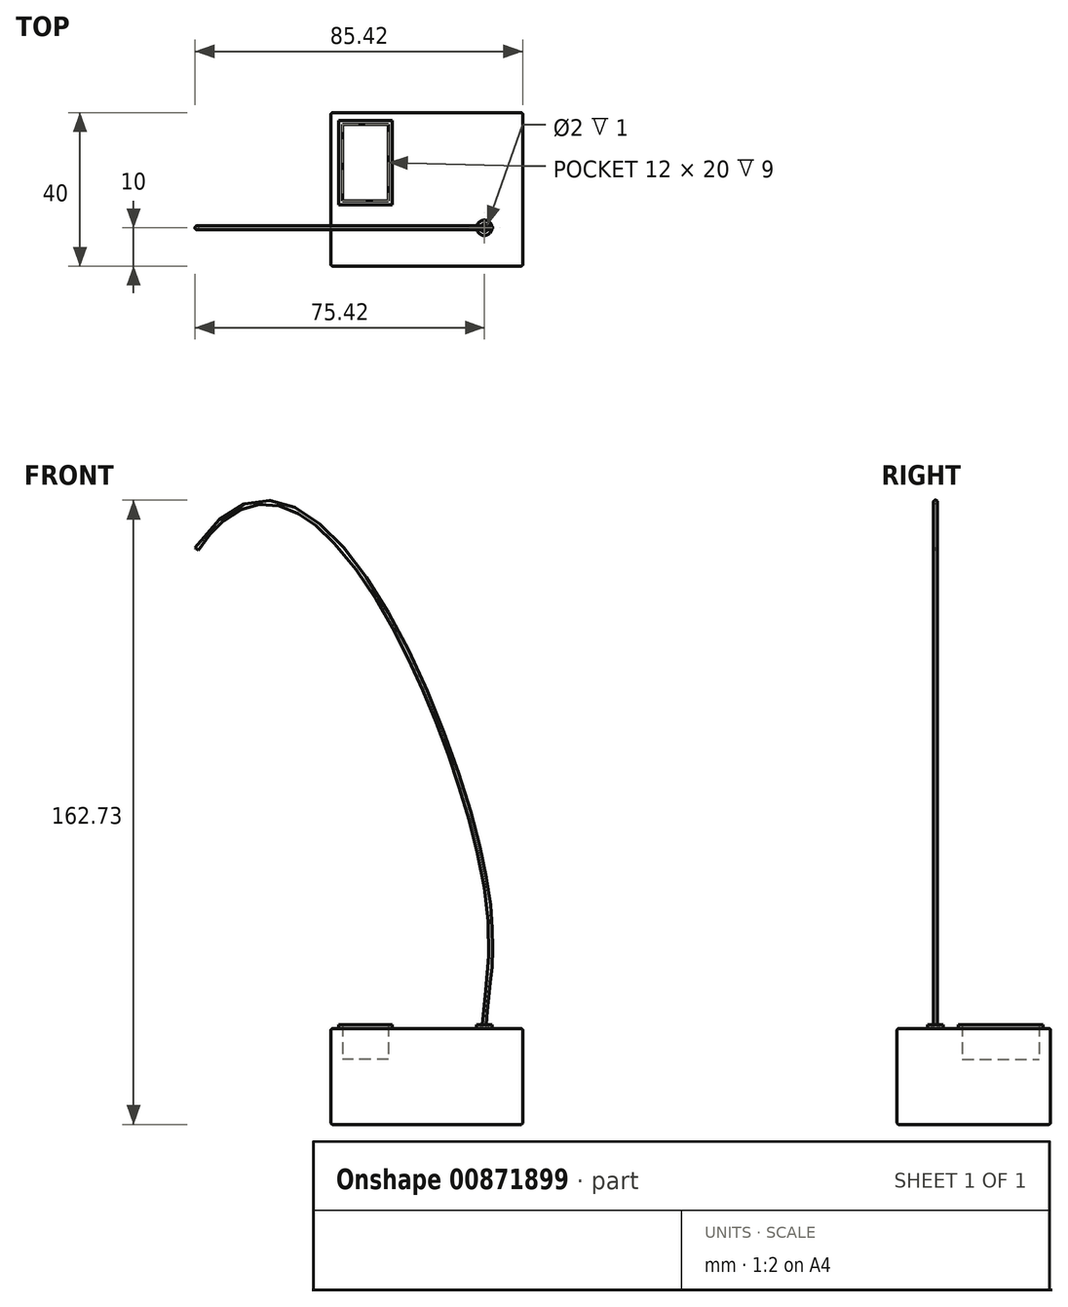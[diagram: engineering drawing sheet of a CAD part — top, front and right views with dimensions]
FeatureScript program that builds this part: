
annotation { "Feature Type Name" : "Feature", "Feature Type Description" : "" }
export const myFeature = defineFeature(function(context is Context, id is Id, definition is map)
    precondition{}
    {
        {
            var Q0;
            Q0=qCreatedBy(makeId("Top.planeOp"),FACE);
            var sketch = newSketch(context, id + "F0", { "sketchPlane" : qUnion([Q0])});
            skLineSegment(sketch, "E0.bottom", {"start": v(25, -20) * mm, "end": v(-25, -20) * mm});
            skLineSegment(sketch, "E0.top", {"start": v(25, 20) * mm, "end": v(-25, 20) * mm});
            skLineSegment(sketch, "E0.left", {"start": v(25, -20) * mm, "end": v(25, 20) * mm});
            skLineSegment(sketch, "E0.right", {"start": v(-25, -20) * mm, "end": v(-25, 20) * mm});
            skPoint(sketch, "E0.middle", {"position": v(0, 0) * mm});
            skSolve(sketch);
        }
        {
            var Q0;
            Q0=makeQuery(id+"F0.imprint","IMPRINT",FACE,{"disambiguationData":[TD([[makeQuery(id+"F0.imprint","IMPRINT",EDGE,{"derivedFrom":sQuery(id+"F0.wireOp",EDGE,"E0.bottom")}),-1.0]])]});
            extrude(context, id + "F1", {"entities" : qUnion([Q0]), "depth" : 25 * mm, "offsetDistance" : 25 * mm});
        }
        {
            var Q0;
            Q0=makeQuery(id+"F1.opExtrude","CAP_FACE",FACE,{"disambiguationData":[OSD([sQuery(id+"F0.wireOp",EDGE,"E0.bottom"),sQuery(id+"F0.wireOp",EDGE,"E0.top"),sQuery(id+"F0.wireOp",EDGE,"E0.left"),sQuery(id+"F0.wireOp",EDGE,"E0.right")])],"isStart":false});
            var sketch = newSketch(context, id + "F2", { "sketchPlane" : qUnion([Q0])});
            skLineSegment(sketch, "E1.bottom", {"start": v(-9, 18) * mm, "end": v(-23, 18) * mm});
            skLineSegment(sketch, "E1.top", {"start": v(-9, -4) * mm, "end": v(-23, -4) * mm});
            skLineSegment(sketch, "E1.left", {"start": v(-9, 18) * mm, "end": v(-9, -4) * mm});
            skLineSegment(sketch, "E1.right", {"start": v(-23, 18) * mm, "end": v(-23, -4) * mm});
            skPoint(sketch, "E1.middle", {"position": v(-16, 7) * mm});
            skLineSegment(sketch, "E2.bottom", {"start": v(-10, -3) * mm, "end": v(-22, -3) * mm});
            skLineSegment(sketch, "E2.top", {"start": v(-10, 17) * mm, "end": v(-22, 17) * mm});
            skLineSegment(sketch, "E2.left", {"start": v(-10, -3) * mm, "end": v(-10, 17) * mm});
            skLineSegment(sketch, "E2.right", {"start": v(-22, -3) * mm, "end": v(-22, 17) * mm});
            skCircle(sketch, "E3", {"center": v(15, -10) * mm, "radius": 2 * mm});
            skCircle(sketch, "E4", {"center": v(15, -10) * mm, "radius": 1 * mm});
            skSolve(sketch);
        }
        {
            var Q0;
            Q0=qSketchRegion(id+"F2",true);
            extrude(context, id + "F3", {"entities" : qUnion([Q0]), "operationType" : NewBodyOperationType.ADD, "depth" : 1 * mm, "offsetDistance" : 25 * mm});
        }
        {
            var Q0;
            Q0=makeQuery(id+"F3.boolean.opBoolean","SPLIT",FACE,{"disambiguationData":[TD([makeQuery(id+"F3.opExtrude","SWEPT_FACE",FACE,{"disambiguationData":[OSD([sQuery(id+"F2.wireOp",EDGE,"E2.bottom")])]})])],"derivedFrom":makeQuery(id+"F1.opExtrude","CAP_FACE",FACE,{"disambiguationData":[OSD([sQuery(id+"F0.wireOp",EDGE,"E0.bottom"),sQuery(id+"F0.wireOp",EDGE,"E0.top"),sQuery(id+"F0.wireOp",EDGE,"E0.left"),sQuery(id+"F0.wireOp",EDGE,"E0.right")])],"isStart":false})});
            extrude(context, id + "F4", {"entities" : qUnion([Q0]), "operationType" : NewBodyOperationType.REMOVE, "oppositeDirection" : true, "depth" : 8 * mm, "offsetDistance" : 25 * mm});
        }
        {
            var Q0;
            Q0=makeQuery(id+"F1.opExtrude","SWEPT_FACE",FACE,{"disambiguationData":[OSD([sQuery(id+"F0.wireOp",EDGE,"E0.bottom")])]});
            cPlane(context, id + "F5", {"entities" : qUnion([Q0]), "cplaneType" : CPlaneType.OFFSET, "offset" : 10 * mm, "oppositeDirection" : true, "width" : 150 * mm, "height" : 150 * mm});
        }
        {
            var Q0;
            Q0=qCreatedBy(id+"F5.planeOp",FACE);
            var sketch = newSketch(context, id + "F6", { "sketchPlane" : qUnion([Q0])});
            skLineSegment(sketch, "E5.0", {"start": v(13, 25) * mm, "end": v(17, 25) * mm, "construction": true});
            skFitSpline(sketch, "E6", {"points": [v(15, 25) * mm, v(13.23, 72.74) * mm, v(-60, 150) * mm], "startDerivative": vector(0, 83.51) * mm, "endDerivative": vector(-143.19, -213.8) * mm});
            skLineSegment(sketch, "E7", {"start": v(15, 25) * mm, "end": v(15, 12.73) * mm, "construction": true});
            skSolve(sketch);
        }
        {
            var Q0;
            {var subQ0=sQuery(id+"F0.wireOp",EDGE,"E0.left");var subQ1=sQuery(id+"F0.wireOp",EDGE,"E0.top");var subQ2=sQuery(id+"F0.wireOp",EDGE,"E0.right");var subQ3=sQuery(id+"F0.wireOp",EDGE,"E0.bottom");Q0=makeQuery(id+"F3.boolean.opBoolean","SPLIT",FACE,{"disambiguationData":[TD([makeQuery(id+"F1.opExtrude","SWEPT_FACE",FACE,{"disambiguationData":[OSD([subQ3])]})])],"derivedFrom":makeQuery(id+"F1.opExtrude","CAP_FACE",FACE,{"disambiguationData":[OSD([subQ3,subQ1,subQ0,subQ2])],"isStart":false})});}
            var sketch = newSketch(context, id + "F7", { "sketchPlane" : qUnion([Q0])});
            skCircle(sketch, "E8", {"center": v(15, -10) * mm, "radius": 0.5 * mm});
            skSolve(sketch);
        }
        {
            var Q0;
            Q0=qSketchRegion(id+"F7",true);
            var Q1;
            Q1=sQuery(id+"F6.wireOp",EDGE,"E6");
            var Q2;
            Q2=sQuery(id+"F6.wireOp",EDGE,"E6");
            sweep(context, id + "F8", {"operationType" : NewBodyOperationType.ADD, "profiles" : qUnion([Q0]), "surfaceProfiles" : qUnion([Q1]), "path" : qUnion([Q2])});
        }
        {
            var Q0;
            Q0=makeQuery(id+"F1.opExtrude","CAP_EDGE",EDGE,{"disambiguationData":[OSD([sQuery(id+"F0.wireOp",EDGE,"E0.top")])],"isStart":false});
            var Q1;
            Q1=makeQuery(id+"F1.opExtrude","CAP_EDGE",EDGE,{"disambiguationData":[OSD([sQuery(id+"F0.wireOp",EDGE,"E0.left")])],"isStart":false});
            var Q2;
            Q2=makeQuery(id+"F1.opExtrude","CAP_EDGE",EDGE,{"disambiguationData":[OSD([sQuery(id+"F0.wireOp",EDGE,"E0.bottom")])],"isStart":false});
            var Q3;
            Q3=makeQuery(id+"F1.opExtrude","CAP_EDGE",EDGE,{"disambiguationData":[OSD([sQuery(id+"F0.wireOp",EDGE,"E0.right")])],"isStart":false});
            var Q4;
            Q4=makeQuery(id+"F1.opExtrude","SWEPT_EDGE",EDGE,{"disambiguationData":[OSD([sQuery(id+"F0.wireOp",EDGE,"E0.top"),sQuery(id+"F0.wireOp",EDGE,"E0.right")])]});
            var Q5;
            Q5=makeQuery(id+"F1.opExtrude","SWEPT_EDGE",EDGE,{"disambiguationData":[OSD([sQuery(id+"F0.wireOp",EDGE,"E0.top"),sQuery(id+"F0.wireOp",EDGE,"E0.left")])]});
            var Q6;
            Q6=makeQuery(id+"F1.opExtrude","SWEPT_EDGE",EDGE,{"disambiguationData":[OSD([sQuery(id+"F0.wireOp",EDGE,"E0.bottom"),sQuery(id+"F0.wireOp",EDGE,"E0.left")])]});
            var Q7;
            Q7=makeQuery(id+"F1.opExtrude","SWEPT_EDGE",EDGE,{"disambiguationData":[OSD([sQuery(id+"F0.wireOp",EDGE,"E0.bottom"),sQuery(id+"F0.wireOp",EDGE,"E0.right")])]});
            var Q8;
            Q8=makeQuery(id+"F1.opExtrude","CAP_FACE",FACE,{"disambiguationData":[OSD([sQuery(id+"F0.wireOp",EDGE,"E0.bottom"),sQuery(id+"F0.wireOp",EDGE,"E0.top"),sQuery(id+"F0.wireOp",EDGE,"E0.left"),sQuery(id+"F0.wireOp",EDGE,"E0.right")])],"isStart":true});
            fillet(context, id + "F9", {"entities" : qUnion([Q0, Q1, Q2, Q3, Q4, Q5, Q6, Q7, Q8]), "radius" : 0.5 * mm, "tangentPropagation" : true, "allowEdgeOverflow" : false});
        }
    });
